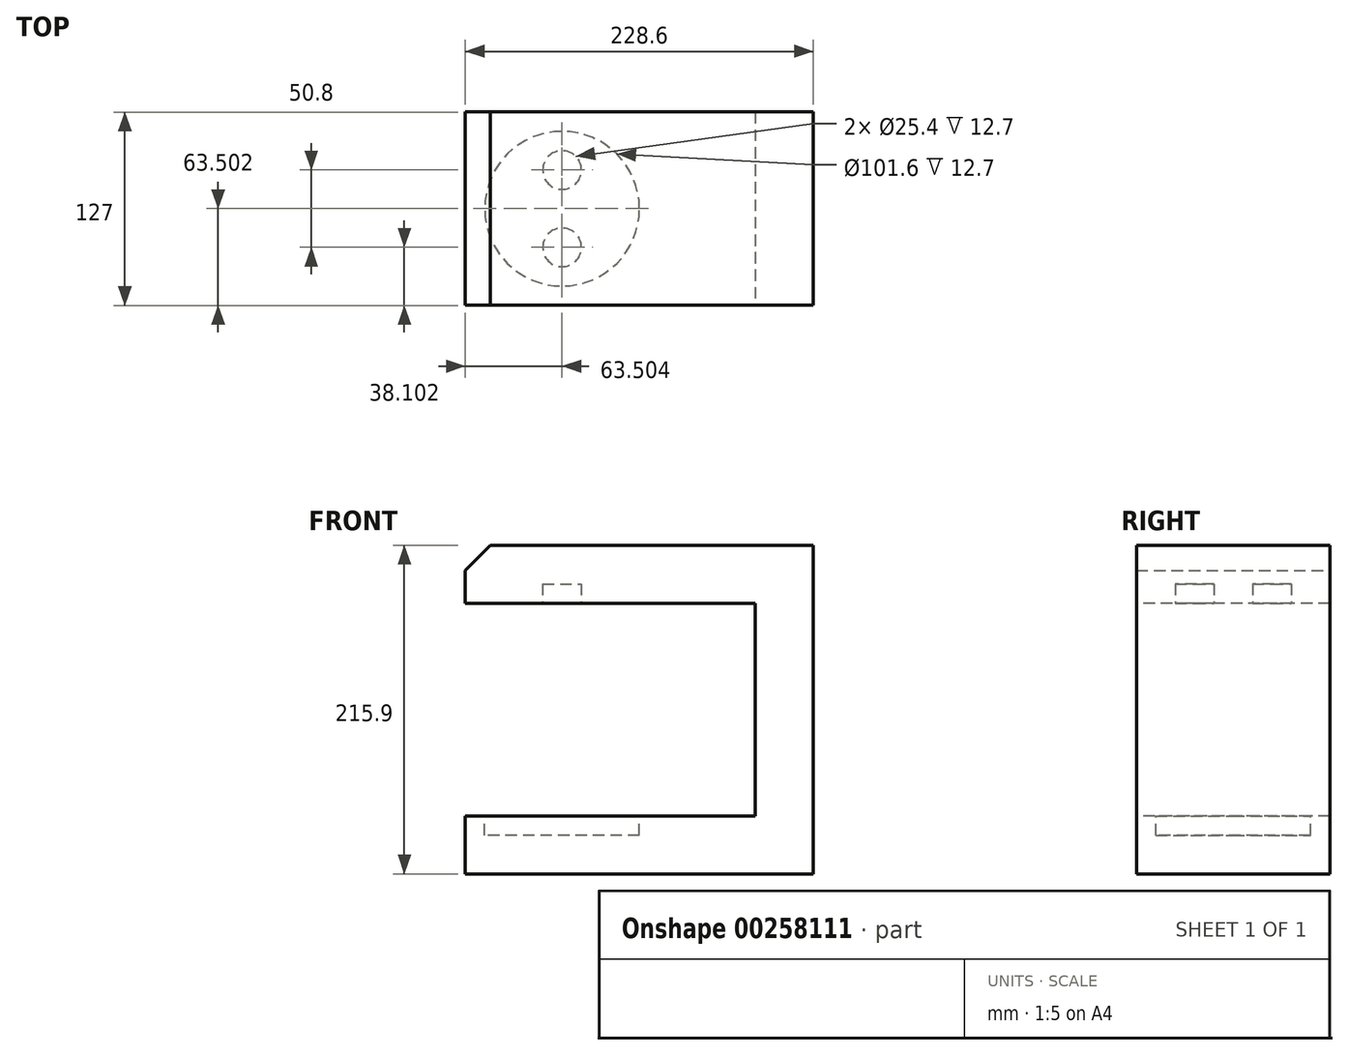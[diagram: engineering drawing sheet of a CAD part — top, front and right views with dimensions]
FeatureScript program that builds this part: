
annotation { "Feature Type Name" : "Feature", "Feature Type Description" : "" }
export const myFeature = defineFeature(function(context is Context, id is Id, definition is map)
    precondition{}
    {
        {
            var Q0;
            Q0=qCreatedBy(makeId("Top.planeOp"),FACE);
            var sketch = newSketch(context, id + "F0", { "sketchPlane" : qUnion([Q0])});
            skLineSegment(sketch, "E0.bottom", {"start": v(-48.08, 138.06) * mm, "end": v(180.52, 138.06) * mm});
            skLineSegment(sketch, "E0.top", {"start": v(-48.08, 11.06) * mm, "end": v(180.52, 11.06) * mm});
            skLineSegment(sketch, "E0.left", {"start": v(-48.08, 138.06) * mm, "end": v(-48.08, 11.06) * mm});
            skLineSegment(sketch, "E0.right", {"start": v(180.52, 138.06) * mm, "end": v(180.52, 11.06) * mm});
            skSolve(sketch);
        }
        {
            var Q0;
            Q0=makeQuery(id+"F0.imprint","IMPRINT",FACE,{"disambiguationData":[TD([[makeQuery(id+"F0.imprint","IMPRINT",EDGE,{"derivedFrom":sQuery(id+"F0.wireOp",EDGE,"E0.bottom")}),-1.0]])]});
            extrude(context, id + "F1", {"entities" : qUnion([Q0]), "depth" : 38.1 * mm});
        }
        {
            var Q0;
            Q0=makeQuery(id+"F1.opExtrude","CAP_FACE",FACE,{"disambiguationData":[OSD([sQuery(id+"F0.wireOp",EDGE,"E0.bottom"),sQuery(id+"F0.wireOp",EDGE,"E0.top"),sQuery(id+"F0.wireOp",EDGE,"E0.left"),sQuery(id+"F0.wireOp",EDGE,"E0.right")])],"isStart":false});
            var sketch = newSketch(context, id + "F2", { "sketchPlane" : qUnion([Q0])});
            skLineSegment(sketch, "E1", {"start": v(142.42, 138.06) * mm, "end": v(142.42, 11.06) * mm});
            skLineSegment(sketch, "E2", {"start": v(142.42, 11.06) * mm, "end": v(180.52, 11.06) * mm});
            skLineSegment(sketch, "E3", {"start": v(180.52, 11.06) * mm, "end": v(180.52, 138.06) * mm});
            skLineSegment(sketch, "E4", {"start": v(180.52, 138.06) * mm, "end": v(142.42, 138.06) * mm});
            skSolve(sketch);
        }
        {
            var Q0;
            Q0 = qSketchRegion(id + "F2", true);
            extrude(context, id + "F3", {"entities" : qUnion([Q0]), "operationType" : NewBodyOperationType.ADD, "depth" : 139.7 * mm});
        }
        {
            var Q0;
            Q0=makeQuery(id+"F3.opExtrude","CAP_FACE",FACE,{"disambiguationData":[OSD([sQuery(id+"F2.wireOp",EDGE,"E1"),sQuery(id+"F2.wireOp",EDGE,"E2"),sQuery(id+"F2.wireOp",EDGE,"E3"),sQuery(id+"F2.wireOp",EDGE,"E4")])],"isStart":false});
            var sketch = newSketch(context, id + "F4", { "sketchPlane" : qUnion([Q0])});
            skLineSegment(sketch, "E5.bottom", {"start": v(180.52, 138.06) * mm, "end": v(-48.08, 138.06) * mm});
            skLineSegment(sketch, "E5.top", {"start": v(180.52, 11.06) * mm, "end": v(-48.08, 11.06) * mm});
            skLineSegment(sketch, "E5.left", {"start": v(180.52, 138.06) * mm, "end": v(180.52, 11.06) * mm});
            skLineSegment(sketch, "E5.right", {"start": v(-48.08, 138.06) * mm, "end": v(-48.08, 11.06) * mm});
            skSolve(sketch);
        }
        {
            var Q0;
            Q0 = qSketchRegion(id + "F4", true);
            extrude(context, id + "F5", {"entities" : qUnion([Q0]), "operationType" : NewBodyOperationType.ADD, "depth" : 38.1 * mm});
        }
        {
            var Q0;
            Q0=makeQuery(id+"F5.opExtrude","CAP_EDGE",EDGE,{"disambiguationData":[OSD([sQuery(id+"F4.wireOp",EDGE,"E5.right")])],"isStart":false});
            chamfer(context, id + "F6", {"entities" : qUnion([Q0]), "width" : 16.5 * mm, "tangentPropagation" : true});
        }
        {
            var Q0;
            Q0=makeQuery(id+"F5.opExtrude","CAP_FACE",FACE,{"disambiguationData":[OSD([sQuery(id+"F4.wireOp",EDGE,"E5.bottom"),sQuery(id+"F4.wireOp",EDGE,"E5.top"),sQuery(id+"F4.wireOp",EDGE,"E5.left"),sQuery(id+"F4.wireOp",EDGE,"E5.right")])],"isStart":true});
            var sketch = newSketch(context, id + "F7", { "sketchPlane" : qUnion([Q0])});
            skCircle(sketch, "E6", {"center": v(15.42, -99.96) * mm, "radius": 12.7 * mm});
            skCircle(sketch, "E7", {"center": v(15.42, -49.16) * mm, "radius": 12.7 * mm});
            skSolve(sketch);
        }
        {
            var Q0;
            Q0=makeQuery(id+"F7.imprint","IMPRINT",FACE,{"disambiguationData":[TD([[makeQuery(id+"F7.imprint","IMPRINT",EDGE,{"derivedFrom":sQuery(id+"F7.wireOp",EDGE,"E6")}),1.0]])]});
            extrude(context, id + "F8", {"entities" : qUnion([Q0]), "operationType" : NewBodyOperationType.REMOVE, "oppositeDirection" : true, "depth" : 12.7 * mm});
        }
        {
            var Q0;
            Q0=makeQuery(id+"F7.imprint","IMPRINT",FACE,{"disambiguationData":[TD([[makeQuery(id+"F7.imprint","IMPRINT",EDGE,{"derivedFrom":sQuery(id+"F7.wireOp",EDGE,"E7")}),1.0]])]});
            extrude(context, id + "F9", {"entities" : qUnion([Q0]), "operationType" : NewBodyOperationType.REMOVE, "oppositeDirection" : true, "depth" : 12.7 * mm});
        }
        {
            var Q0;
            Q0=makeQuery(id+"F1.opExtrude","CAP_FACE",FACE,{"disambiguationData":[OSD([sQuery(id+"F0.wireOp",EDGE,"E0.bottom"),sQuery(id+"F0.wireOp",EDGE,"E0.top"),sQuery(id+"F0.wireOp",EDGE,"E0.left"),sQuery(id+"F0.wireOp",EDGE,"E0.right")])],"isStart":false});
            var sketch = newSketch(context, id + "F10", { "sketchPlane" : qUnion([Q0])});
            skCircle(sketch, "E8", {"center": v(15.42, 74.56) * mm, "radius": 50.8 * mm});
            skSolve(sketch);
        }
        {
            var Q0;
            Q0=makeQuery(id+"F10.imprint","IMPRINT",FACE,{"disambiguationData":[TD([[makeQuery(id+"F10.imprint","IMPRINT",EDGE,{"derivedFrom":sQuery(id+"F10.wireOp",EDGE,"E8")}),1.0]])]});
            extrude(context, id + "F11", {"entities" : qUnion([Q0]), "operationType" : NewBodyOperationType.REMOVE, "oppositeDirection" : true, "depth" : 12.7 * mm});
        }
    });
